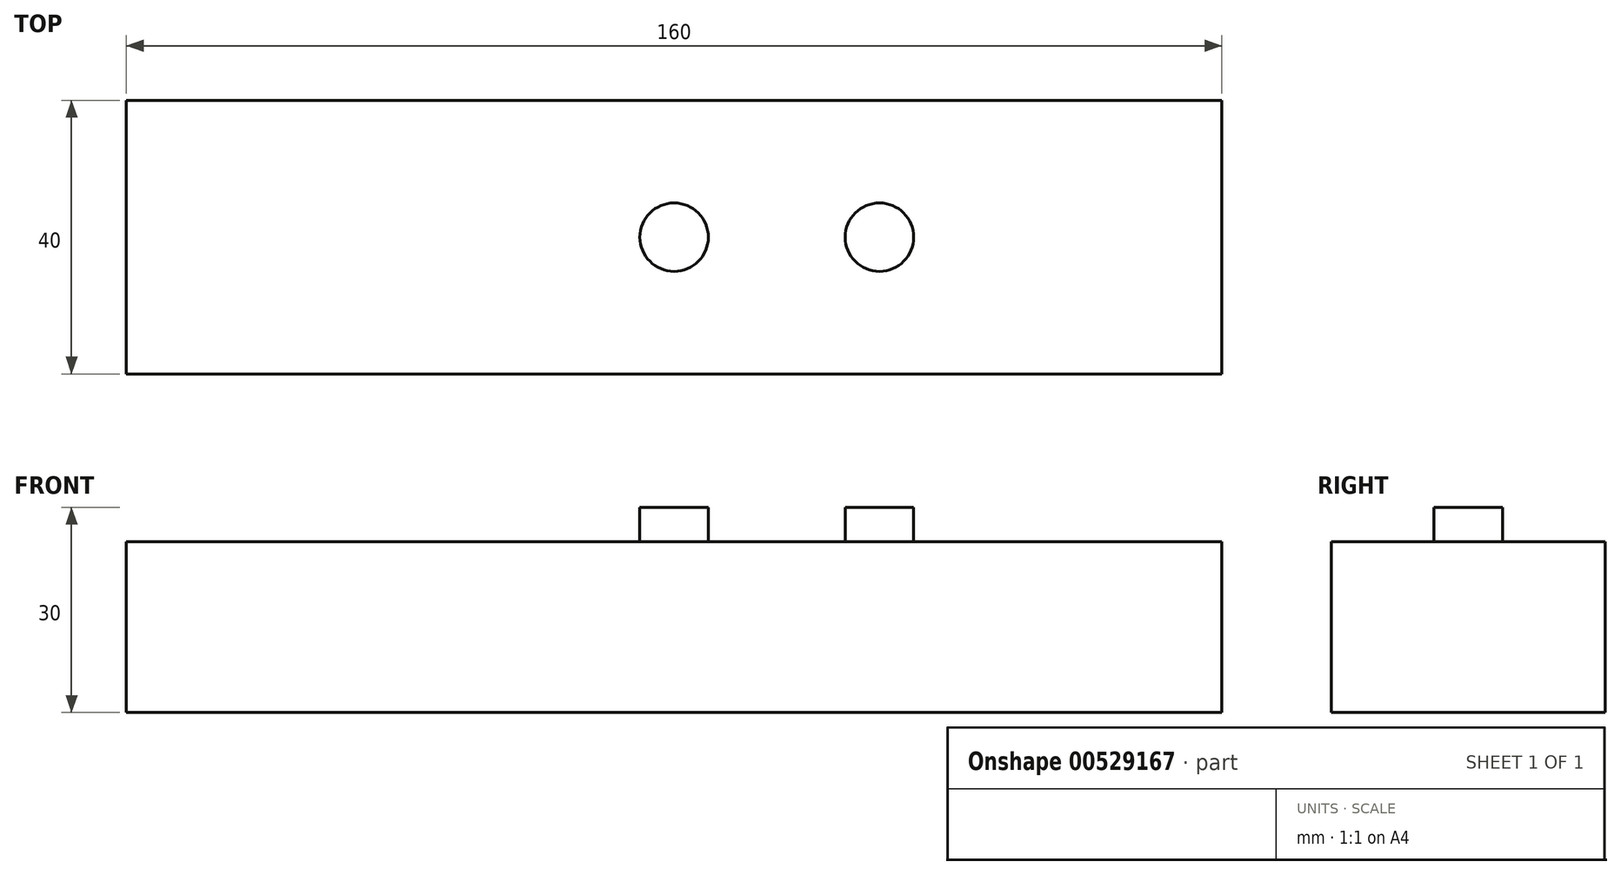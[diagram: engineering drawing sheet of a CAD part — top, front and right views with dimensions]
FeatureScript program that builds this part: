
annotation { "Feature Type Name" : "Feature", "Feature Type Description" : "" }
export const myFeature = defineFeature(function(context is Context, id is Id, definition is map)
    precondition{}
    {
        {
            var Q0;
            Q0=qCreatedBy(makeId("Top.planeOp"),FACE);
            var sketch = newSketch(context, id + "F0", { "sketchPlane" : qUnion([Q0])});
            skLineSegment(sketch, "E0.bottom", {"start": v(-80, 20) * mm, "end": v(80, 20) * mm});
            skLineSegment(sketch, "E0.top", {"start": v(-80, -20) * mm, "end": v(80, -20) * mm});
            skLineSegment(sketch, "E0.left", {"start": v(-80, 20) * mm, "end": v(-80, -20) * mm});
            skLineSegment(sketch, "E0.right", {"start": v(80, 20) * mm, "end": v(80, -20) * mm});
            skPoint(sketch, "E0.middle", {"position": v(0, 0) * mm});
            skSolve(sketch);
        }
        {
            var Q0;
            Q0=makeQuery(id+"F0.imprint","IMPRINT",FACE,{"disambiguationData":[TD([[makeQuery(id+"F0.imprint","IMPRINT",EDGE,{"derivedFrom":sQuery(id+"F0.wireOp",EDGE,"E0.bottom")}),-1.0]])]});
            extrude(context, id + "F1", {"entities" : qUnion([Q0]), "depth" : 25 * mm, "offsetDistance" : 25 * mm});
        }
        {
            var Q0;
            Q0=makeQuery(id+"F1.opExtrude","CAP_FACE",FACE,{"disambiguationData":[OSD([sQuery(id+"F0.wireOp",EDGE,"E0.bottom"),sQuery(id+"F0.wireOp",EDGE,"E0.top"),sQuery(id+"F0.wireOp",EDGE,"E0.left"),sQuery(id+"F0.wireOp",EDGE,"E0.right")])],"isStart":false});
            var sketch = newSketch(context, id + "F2", { "sketchPlane" : qUnion([Q0])});
            skLineSegment(sketch, "E1", {"start": v(0, 0) * mm, "end": v(30, 0) * mm});
            skCircle(sketch, "E2", {"center": v(0, 0) * mm, "radius": 5 * mm});
            skCircle(sketch, "E3", {"center": v(30, 0) * mm, "radius": 5 * mm});
            skSolve(sketch);
        }
        {
            var Q0;
            Q0=makeQuery(id+"F2.imprint","IMPRINT",FACE,{"disambiguationData":[TD([[makeQuery(id+"F2.imprint","IMPRINT",EDGE,{"derivedFrom":sQuery(id+"F2.wireOp",EDGE,"E2")}),1.0]])]});
            var Q1;
            Q1=makeQuery(id+"F2.imprint","IMPRINT",FACE,{"disambiguationData":[TD([[makeQuery(id+"F2.imprint","IMPRINT",EDGE,{"derivedFrom":sQuery(id+"F2.wireOp",EDGE,"E3")}),1.0]])]});
            extrude(context, id + "F3", {"entities" : qUnion([Q0, Q1]), "operationType" : NewBodyOperationType.ADD, "depth" : 5 * mm, "offsetDistance" : 25 * mm});
        }
    });
